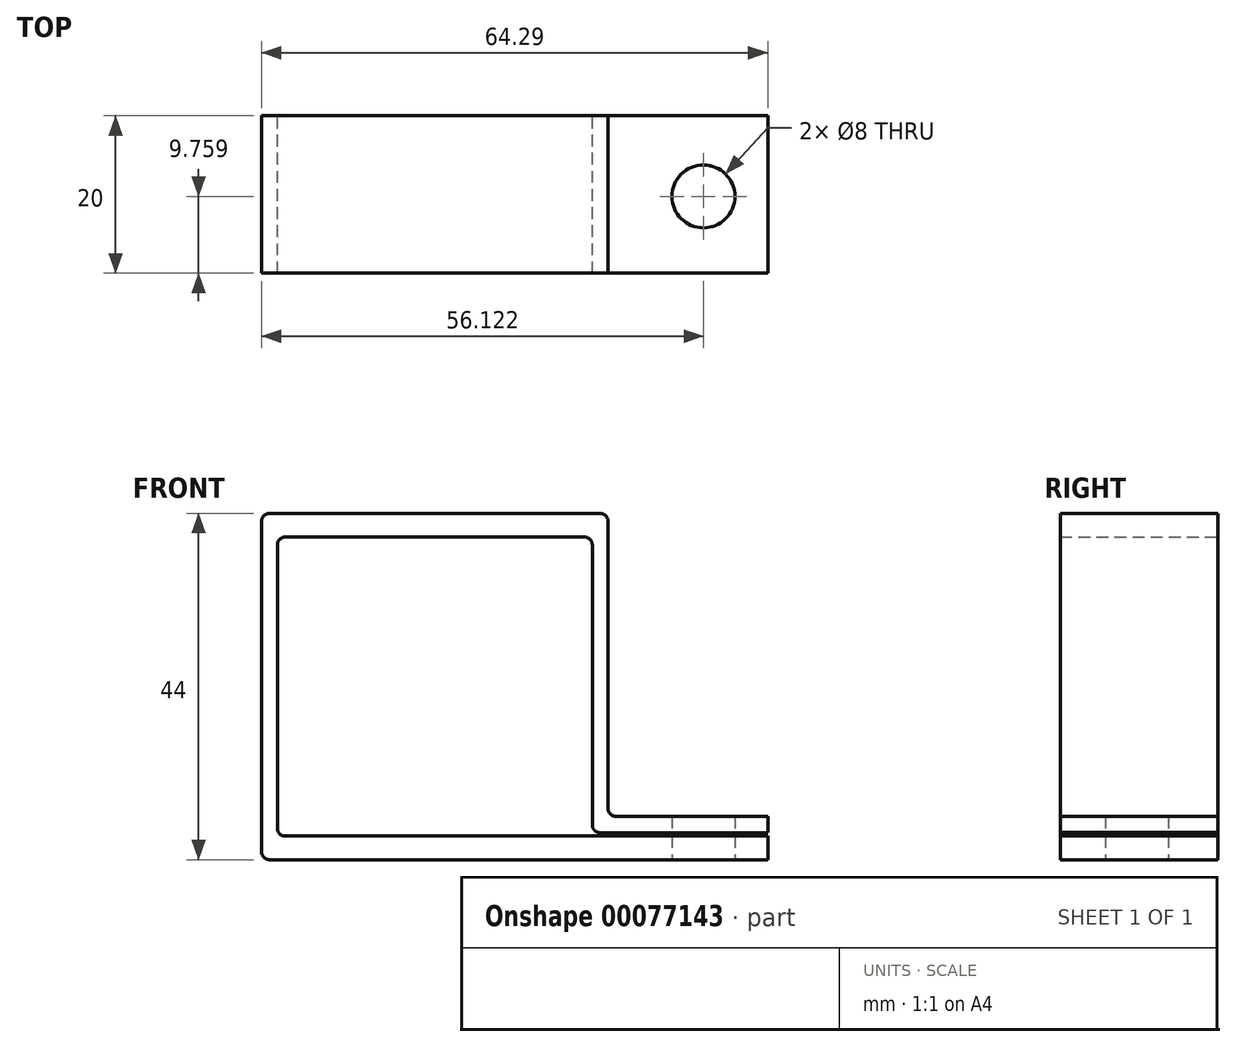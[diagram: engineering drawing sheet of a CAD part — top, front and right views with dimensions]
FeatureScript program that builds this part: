
annotation { "Feature Type Name" : "Feature", "Feature Type Description" : "" }
export const myFeature = defineFeature(function(context is Context, id is Id, definition is map)
    precondition{}
    {
        {
            var Q0;
            Q0=qCreatedBy(makeId("Front.planeOp"),FACE);
            var sketch = newSketch(context, id + "F0", { "sketchPlane" : qUnion([Q0])});
            skLineSegment(sketch, "E0", {"start": v(20.3, 0) * mm, "end": v(-44, 0) * mm});
            skLineSegment(sketch, "E1", {"start": v(-44, 0) * mm, "end": v(-44, 44) * mm});
            skLineSegment(sketch, "E2", {"start": v(-44, 44) * mm, "end": v(0, 44) * mm});
            skLineSegment(sketch, "E3", {"start": v(0, 44) * mm, "end": v(0, 5.5) * mm});
            skLineSegment(sketch, "E4", {"start": v(20.3, 5.5) * mm, "end": v(20.3, 3.5) * mm});
            skLineSegment(sketch, "E5", {"start": v(-2, 41) * mm, "end": v(-42, 41) * mm});
            skLineSegment(sketch, "E6", {"start": v(-42, 41) * mm, "end": v(-42, 3) * mm});
            skLineSegment(sketch, "E7", {"start": v(-42, 3) * mm, "end": v(-2, 3) * mm});
            skLineSegment(sketch, "E8", {"start": v(20.3, 3) * mm, "end": v(20.3, 0) * mm});
            skLineSegment(sketch, "E9", {"start": v(-2, 3.42) * mm, "end": v(-2, 41) * mm});
            skPoint(sketch, "E10.end.orphan", {"position": v(20.3, 1.5) * mm});
            skLineSegment(sketch, "E11", {"start": v(-2, 3) * mm, "end": v(20.3, 3) * mm});
            skLineSegment(sketch, "E12", {"start": v(20.3, 3.5) * mm, "end": v(-2, 3.42) * mm});
            skLineSegment(sketch, "E13", {"start": v(20.3, 5.5) * mm, "end": v(0, 5.5) * mm});
            skSolve(sketch);
        }
        {
            var Q0;
            Q0=makeQuery(id+"F0.imprint","IMPRINT",FACE,{"disambiguationData":[TD([[makeQuery(id+"F0.imprint","IMPRINT",EDGE,{"derivedFrom":sQuery(id+"F0.wireOp",EDGE,"E0")}),-1.0]])]});
            extrude(context, id + "F1", {"entities" : qUnion([Q0]), "depth" : 20 * mm, "offsetDistance" : 25 * mm});
        }
        {
            var Q0;
            Q0=makeQuery(id+"F1.opExtrude","SWEPT_EDGE",EDGE,{"disambiguationData":[OSD([sQuery(id+"F0.wireOp",EDGE,"E5"),sQuery(id+"F0.wireOp",EDGE,"E9")])]});
            var Q1;
            Q1=makeQuery(id+"F1.opExtrude","SWEPT_EDGE",EDGE,{"disambiguationData":[OSD([sQuery(id+"F0.wireOp",EDGE,"E5"),sQuery(id+"F0.wireOp",EDGE,"E6")])]});
            var Q2;
            Q2=makeQuery(id+"F1.opExtrude","SWEPT_EDGE",EDGE,{"disambiguationData":[OSD([sQuery(id+"F0.wireOp",EDGE,"E6"),sQuery(id+"F0.wireOp",EDGE,"E7")])]});
            var Q3;
            Q3=makeQuery(id+"F1.opExtrude","SWEPT_EDGE",EDGE,{"disambiguationData":[OSD([sQuery(id+"F0.wireOp",EDGE,"E3"),sQuery(id+"F0.wireOp",EDGE,"E13")])]});
            var Q4;
            Q4=makeQuery(id+"F1.opExtrude","SWEPT_EDGE",EDGE,{"disambiguationData":[OSD([sQuery(id+"F0.wireOp",EDGE,"E2"),sQuery(id+"F0.wireOp",EDGE,"E3")])]});
            var Q5;
            Q5=makeQuery(id+"F1.opExtrude","SWEPT_EDGE",EDGE,{"disambiguationData":[OSD([sQuery(id+"F0.wireOp",EDGE,"E1"),sQuery(id+"F0.wireOp",EDGE,"E2")])]});
            var Q6;
            Q6=makeQuery(id+"F1.opExtrude","SWEPT_EDGE",EDGE,{"disambiguationData":[OSD([sQuery(id+"F0.wireOp",EDGE,"E0"),sQuery(id+"F0.wireOp",EDGE,"E1")])]});
            var Q7;
            Q7=makeQuery(id+"F1.opExtrude","SWEPT_EDGE",EDGE,{"disambiguationData":[OSD([sQuery(id+"F0.wireOp",EDGE,"E9"),sQuery(id+"F0.wireOp",EDGE,"E12")])]});
            fillet(context, id + "F2", {"entities" : qUnion([Q0, Q1, Q2, Q3, Q4, Q5, Q6, Q7]), "radius" : 1 * mm, "tangentPropagation" : true, "allowEdgeOverflow" : false});
        }
        {
            var Q0;
            Q0=qCreatedBy(makeId("Top.planeOp"),FACE);
            var sketch = newSketch(context, id + "F3", { "sketchPlane" : qUnion([Q0])});
            skCircle(sketch, "E14", {"center": v(12.12, -10.24) * mm, "radius": 4 * mm});
            skSolve(sketch);
        }
        {
            var Q0;
            Q0=makeQuery(id+"F3.imprint","IMPRINT",FACE,{"disambiguationData":[TD([[makeQuery(id+"F3.imprint","IMPRINT",EDGE,{"derivedFrom":sQuery(id+"F3.wireOp",EDGE,"E14")}),1.0]])]});
            extrude(context, id + "F4", {"entities" : qUnion([Q0]), "operationType" : NewBodyOperationType.REMOVE, "depth" : 23.2 * mm, "offsetDistance" : 25 * mm});
        }
    });
